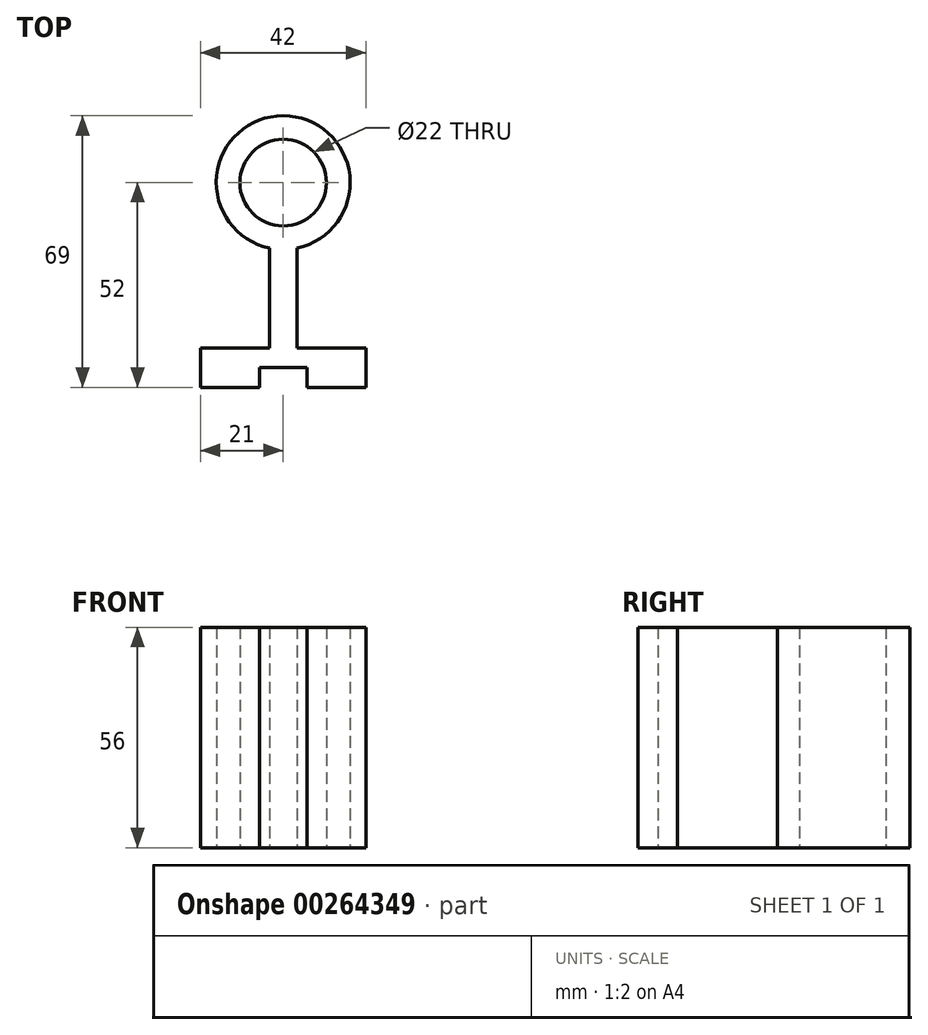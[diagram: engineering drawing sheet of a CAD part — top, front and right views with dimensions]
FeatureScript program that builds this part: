
annotation { "Feature Type Name" : "Feature", "Feature Type Description" : "" }
export const myFeature = defineFeature(function(context is Context, id is Id, definition is map)
    precondition{}
    {
        {
            var Q0;
            Q0=qCreatedBy(makeId("Top.planeOp"),FACE);
            var sketch = newSketch(context, id + "F0", { "sketchPlane" : qUnion([Q0])});
            skLineSegment(sketch, "E0", {"start": v(0, 0) * mm, "end": v(0, 25.36) * mm});
            skLineSegment(sketch, "E1", {"start": v(0, 0) * mm, "end": v(-17.5, 0) * mm});
            skLineSegment(sketch, "E2", {"start": v(-17.5, 0) * mm, "end": v(-17.5, -10) * mm});
            skLineSegment(sketch, "E3", {"start": v(-17.5, -10) * mm, "end": v(-2.5, -10) * mm});
            skLineSegment(sketch, "E4", {"start": v(-2.5, -10) * mm, "end": v(-2.5, -5) * mm});
            skLineSegment(sketch, "E5", {"start": v(-2.5, -5) * mm, "end": v(9.5, -5) * mm});
            skLineSegment(sketch, "E6", {"start": v(9.5, -5) * mm, "end": v(9.5, -10) * mm});
            skLineSegment(sketch, "E7", {"start": v(9.5, -10) * mm, "end": v(24.5, -10) * mm});
            skLineSegment(sketch, "E8", {"start": v(24.5, -10) * mm, "end": v(24.5, 0) * mm});
            skLineSegment(sketch, "E9", {"start": v(24.5, 0) * mm, "end": v(7, 0) * mm});
            skLineSegment(sketch, "E10", {"start": v(7, 0) * mm, "end": v(7, 25.36) * mm});
            skCircle(sketch, "E11", {"center": v(3.5, 42) * mm, "radius": 11 * mm});
            skArc(sketch, "E12", {"start": v(7, 25.36) * mm, "mid": v(3.5, 59) * mm, "end": v(0, 25.36) * mm});
            skSolve(sketch);
        }
        {
            var Q0;
            Q0=makeQuery(id+"F0.imprint","IMPRINT",FACE,{"disambiguationData":[TD([[makeQuery(id+"F0.imprint","IMPRINT",EDGE,{"derivedFrom":sQuery(id+"F0.wireOp",EDGE,"E0")}),-1.0]])]});
            extrude(context, id + "F1", {"entities" : qUnion([Q0]), "depth" : 56 * mm});
        }
    });
